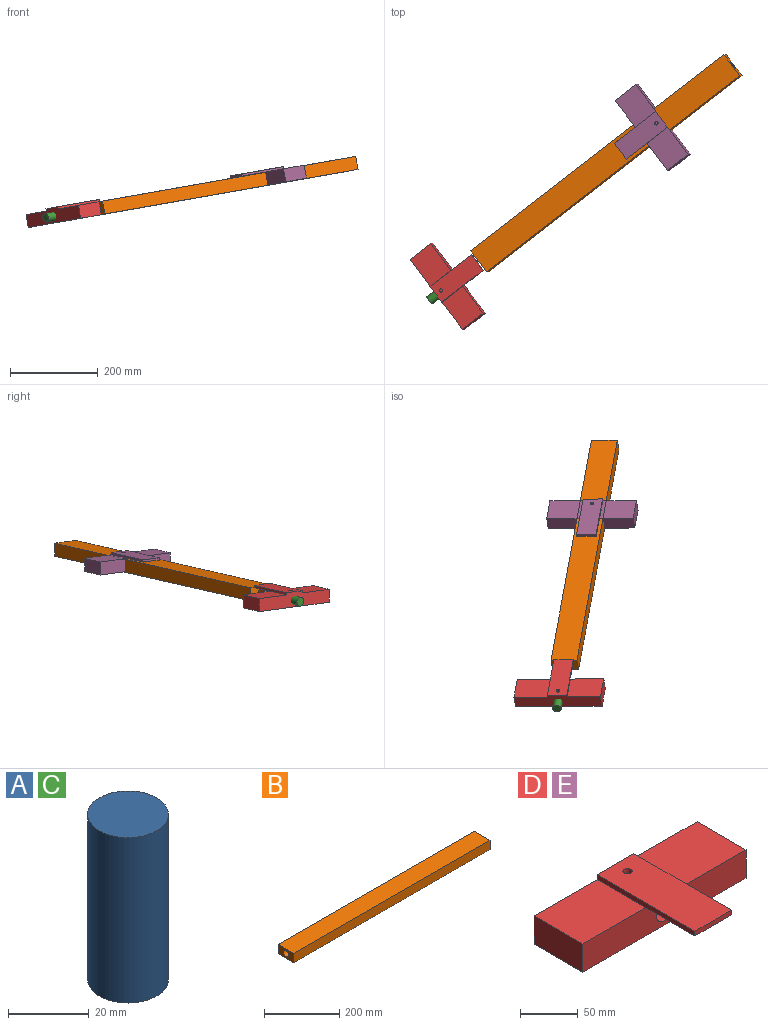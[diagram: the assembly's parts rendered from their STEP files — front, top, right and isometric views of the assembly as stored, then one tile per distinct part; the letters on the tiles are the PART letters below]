
ASSEMBLY  parts=5 mates=4
PART A: 3 faces, bbox 20x20x50 mm
  f0: cylinder r=10mm len=50mm, axis (0,0,-1), area 3141.6mm2, adj f1,f2
  f1: plane 20x20mm, normal (0,0,1), area 314.2mm2, adj f0
  f2: plane 20x20mm, normal (0,0,-1), area 314.2mm2, adj f0
PART B: 10 faces, bbox 736.6x60x30 mm
  f0: plane 736.6x60mm, normal (0,0,1), area 44196mm2, adj f1,f3,f4,f5
  f1: plane 60x30mm, normal (-1,0,0), area 1485.8mm2, adj f0,f2,f4,f5,f6
  f2: plane 736.6x60mm, normal (0,0,-1), area 44196mm2, adj f1,f3,f4,f5
  f3: plane 60x30mm, normal (1,0,0), area 1485.8mm2, adj f0,f2,f4,f5,f8
  f4: plane 736.6x30mm, normal (0,-1,0), area 22098mm2, adj f0,f1,f2,f3
  f5: plane 736.6x30mm, normal (0,1,0), area 22098mm2, adj f0,f1,f2,f3
  f6: cylinder r=10mm len=25mm, axis (-1,0,0), area 1570.8mm2, adj f1,f7
  f7: plane 20x20mm, normal (-1,0,0), area 314.2mm2, adj f6
  f8: cylinder r=10mm len=25mm, axis (1,0,0), area 1570.8mm2, adj f3,f9
  f9: plane 20x20mm, normal (1,0,0), area 314.2mm2, adj f8
PART C: same geometry as A
PART D: 16 faces, bbox 200x120x35 mm
  f0: plane 77.73x60mm, normal (0,0,1), area 4664mm2, adj f4,f5,f6,f10
  f1: plane 77.27x60mm, normal (0,0,1), area 4636mm2, adj f2,f5,f6,f11
  f2: plane 60x30mm, normal (-1,0,0), area 1800mm2, adj f1,f3,f5,f6
  f3: plane 200x60mm, normal (0,0,-1), area 12000mm2, adj f2,f4,f5,f6
  f4: plane 60x30mm, normal (1,0,0), area 1800mm2, adj f0,f3,f5,f6
  f5: plane 200x30mm, normal (0,-1,0), area 5685.8mm2, adj f0,f1,f2,f3,f4,f7,f9
  f6: plane 200x35mm, normal (0,1,0), area 6225mm2, adj f0,f1,f2,f3,f4,f10,f11,f13
  f7: cylinder r=10mm len=25mm, axis (0,-1,0), area 1570.8mm2, adj f5,f8
  f8: plane 20x20mm, normal (0,-1,0), area 314.2mm2, adj f7
  f9: plane 60x45mm, normal (0,0,-1), area 2700mm2, adj f5,f10,f11,f12
  f10: plane 120x5mm, normal (1,0,0), area 600mm2, adj f0,f6,f9,f12,f13
  f11: plane 120x5mm, normal (-1,0,0), area 600mm2, adj f1,f6,f9,f12,f13
  f12: plane 45x5mm, normal (0,-1,0), area 225mm2, adj f9,f10,f11,f13
  f13: plane 120x45mm, normal (0,0,1), area 5349.7mm2, adj f6,f10,f11,f12,f14
  f14: cylinder r=4mm len=8mm, axis (0,0,1), area 125.7mm2, adj f13,f15
  f15: plane 8x8mm, normal (0,0,1), area 50.3mm2, adj f14
PART E: same geometry as D
PLACE A rot(axis=(0.26,-0.91,0.31),105deg) t=(162.95,364.69,58.21)mm
PLACE B rot(axis=(-0.08,-0.25,0.96),38.6deg) t=(-211.84,112.15,-7.88)mm
PLACE C rot(axis=(-0.36,0.89,0.3),86.9deg) t=(-343.42,-27.6,-31.95)mm
PLACE D rot(axis=(-0.09,-0.04,1),127.5deg) t=(-292.79,-57.35,-23.74)mm
PLACE E rot(axis=(0.09,-0.17,-0.98),53.5deg) t=(156.05,428.11,56.27)mm
MATE cylindrical D.f7 <-> C.f0  axis (0.78,0.61,0.14) through (-278.63,22.58,-20.53)mm
MATE cylindrical C.f0 <-> B.f6  axis (-0.78,-0.61,-0.14) through (-323.84,-12.44,-28.5)mm
MATE cylindrical A.f0 <-> B.f8  axis (0.78,0.61,0.14) through (143.38,349.52,54.75)mm
MATE cylindrical E.f7 <-> A.f0  axis (-0.78,-0.61,-0.14) through (151.43,355.77,56.18)mm
